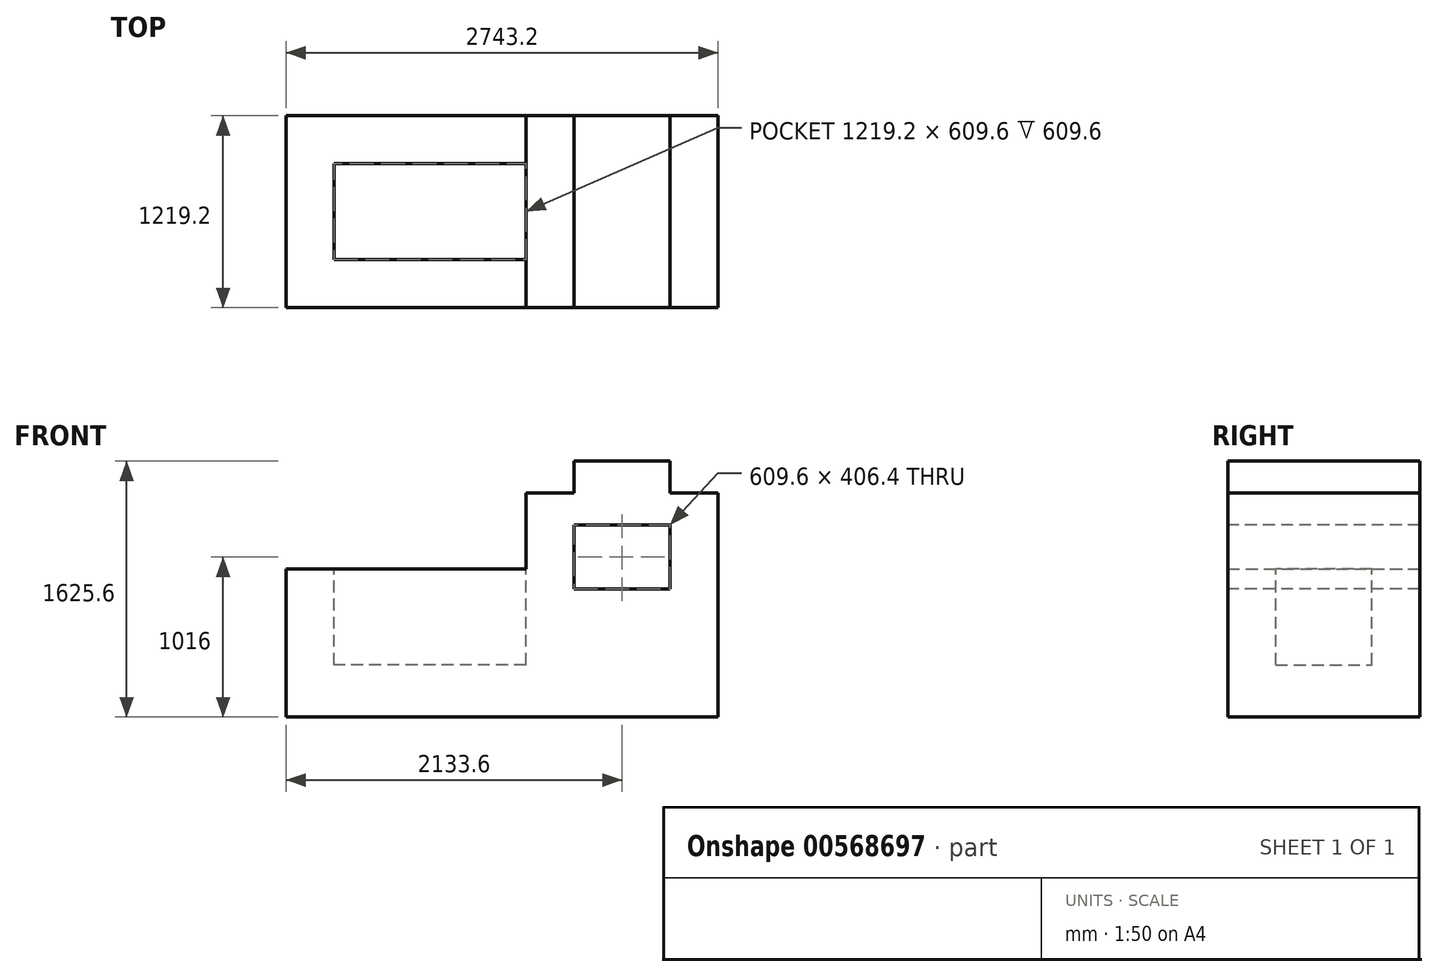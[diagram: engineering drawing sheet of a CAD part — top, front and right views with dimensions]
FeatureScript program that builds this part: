
annotation { "Feature Type Name" : "Feature", "Feature Type Description" : "" }
export const myFeature = defineFeature(function(context is Context, id is Id, definition is map)
    precondition{}
    {
        {
            var Q0;
            Q0=qCreatedBy(makeId("Front.planeOp"),FACE);
            var sketch = newSketch(context, id + "F0", { "sketchPlane" : qUnion([Q0])});
            skLineSegment(sketch, "E0", {"start": v(0, 0) * mm, "end": v(2743.2, 0) * mm});
            skLineSegment(sketch, "E1", {"start": v(2743.2, 0) * mm, "end": v(2743.2, 1422.4) * mm});
            skLineSegment(sketch, "E2", {"start": v(2743.2, 1422.4) * mm, "end": v(2438.4, 1422.4) * mm});
            skLineSegment(sketch, "E3", {"start": v(2438.4, 1422.4) * mm, "end": v(2438.4, 1625.6) * mm});
            skLineSegment(sketch, "E4", {"start": v(2438.4, 1625.6) * mm, "end": v(1828.8, 1625.6) * mm});
            skLineSegment(sketch, "E5", {"start": v(1828.8, 1625.6) * mm, "end": v(1828.8, 1422.4) * mm});
            skLineSegment(sketch, "E6", {"start": v(1828.8, 1422.4) * mm, "end": v(1524, 1422.4) * mm});
            skLineSegment(sketch, "E7", {"start": v(1524, 1422.4) * mm, "end": v(1524, 1117.6) * mm});
            skLineSegment(sketch, "E8", {"start": v(1524, 1117.6) * mm, "end": v(1524, 1422.4) * mm});
            skLineSegment(sketch, "E9", {"start": v(1524, 1201.3) * mm, "end": v(1524, 1422.4) * mm});
            skLineSegment(sketch, "E10", {"start": v(1524, 942.17) * mm, "end": v(1524, 1422.4) * mm});
            skLineSegment(sketch, "E11", {"start": v(1524, 942.17) * mm, "end": v(0, 942.17) * mm});
            skLineSegment(sketch, "E12", {"start": v(0, 942.17) * mm, "end": v(0, 0) * mm});
            skSolve(sketch);
        }
        {
            var Q0;
            Q0=makeQuery(id+"F0.imprint","IMPRINT",FACE,{"disambiguationData":[TD([[makeQuery(id+"F0.imprint","IMPRINT",EDGE,{"derivedFrom":sQuery(id+"F0.wireOp",EDGE,"E0")}),1.0]])]});
            extrude(context, id + "F1", {"entities" : qUnion([Q0]), "depth" : 1219.2 * mm, "offsetDistance" : 25.4 * mm});
        }
        {
            var Q0;
            Q0=makeQuery(id+"F1.opExtrude","SWEPT_FACE",FACE,{"disambiguationData":[OSD([sQuery(id+"F0.wireOp",EDGE,"E11")])]});
            var sketch = newSketch(context, id + "F2", { "sketchPlane" : qUnion([Q0])});
            skLineSegment(sketch, "E13", {"start": v(1524, 0) * mm, "end": v(1524, -304.8) * mm});
            skLineSegment(sketch, "E14", {"start": v(1524, -304.8) * mm, "end": v(304.8, -304.8) * mm});
            skLineSegment(sketch, "E15", {"start": v(304.8, -304.8) * mm, "end": v(304.8, -914.4) * mm});
            skLineSegment(sketch, "E16", {"start": v(304.8, -914.4) * mm, "end": v(1524, -914.4) * mm});
            skLineSegment(sketch, "E17", {"start": v(1524, -914.4) * mm, "end": v(1524, -1219.2) * mm});
            skSolve(sketch);
        }
        {
            var Q0;
            {var subQ0=sQuery(id+"F2.wireOp",EDGE,"E14");Q0=makeQuery(id+"F2.imprint","IMPRINT",FACE,{"disambiguationData":[TD([[makeQuery(id+"F2.imprint","IMPRINT",EDGE,{"derivedFrom":subQ0}),1.0]])]});}
            extrude(context, id + "F3", {"entities" : qUnion([Q0]), "operationType" : NewBodyOperationType.REMOVE, "oppositeDirection" : true, "depth" : 609.6 * mm, "offsetDistance" : 25.4 * mm});
        }
        {
            var Q0;
            Q0=makeQuery(id+"F1.opExtrude","CAP_FACE",FACE,{"disambiguationData":[OSD([sQuery(id+"F0.wireOp",EDGE,"E0"),sQuery(id+"F0.wireOp",EDGE,"E1"),sQuery(id+"F0.wireOp",EDGE,"E2"),sQuery(id+"F0.wireOp",EDGE,"E3"),sQuery(id+"F0.wireOp",EDGE,"E4"),sQuery(id+"F0.wireOp",EDGE,"E5"),sQuery(id+"F0.wireOp",EDGE,"E6"),sQuery(id+"F0.wireOp",EDGE,"E10"),sQuery(id+"F0.wireOp",EDGE,"E11"),sQuery(id+"F0.wireOp",EDGE,"E12")])],"isStart":false});
            var sketch = newSketch(context, id + "F4", { "sketchPlane" : qUnion([Q0])});
            skLineSegment(sketch, "E18", {"start": v(1524, 1422.4) * mm, "end": v(1524, 1219.2) * mm});
            skLineSegment(sketch, "E19", {"start": v(1524, 1219.2) * mm, "end": v(1828.8, 1219.2) * mm});
            skLineSegment(sketch, "E20", {"start": v(1828.8, 1219.2) * mm, "end": v(1828.8, 812.8) * mm});
            skLineSegment(sketch, "E21", {"start": v(1828.8, 812.8) * mm, "end": v(2438.4, 812.8) * mm});
            skLineSegment(sketch, "E22", {"start": v(2438.4, 812.8) * mm, "end": v(2438.4, 1219.2) * mm});
            skLineSegment(sketch, "E23", {"start": v(2438.4, 1219.2) * mm, "end": v(1828.8, 1219.2) * mm});
            skSolve(sketch);
        }
        {
            var Q0;
            Q0=makeQuery(id+"F4.imprint","IMPRINT",FACE,{"disambiguationData":[TD([[makeQuery(id+"F4.imprint","IMPRINT",EDGE,{"derivedFrom":sQuery(id+"F4.wireOp",EDGE,"E20")}),1.0]])]});
            extrude(context, id + "F5", {"entities" : qUnion([Q0]), "operationType" : NewBodyOperationType.REMOVE, "oppositeDirection" : true, "depth" : 1219.2 * mm, "offsetDistance" : 25.4 * mm});
        }
    });
